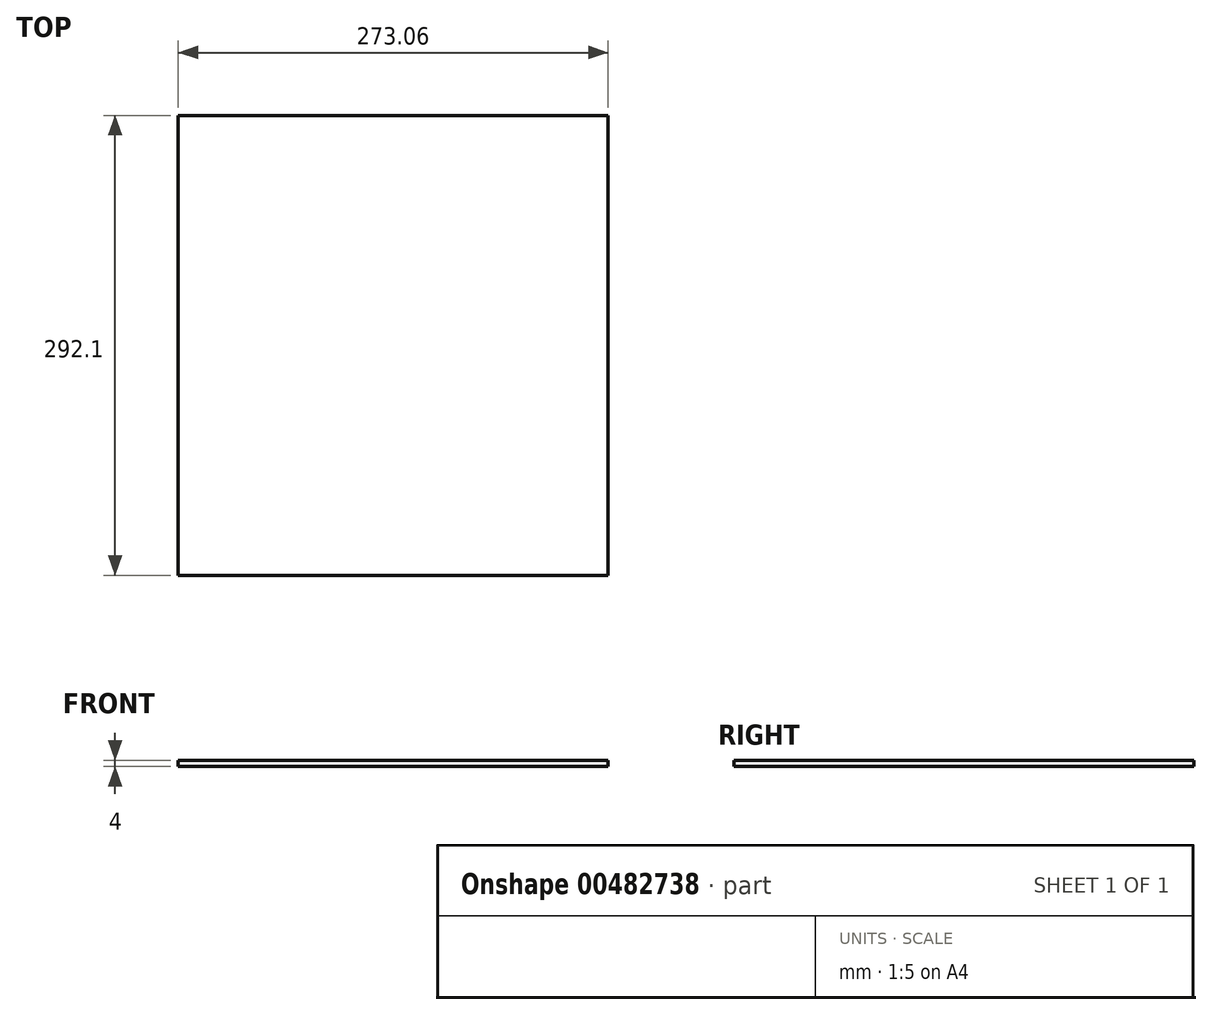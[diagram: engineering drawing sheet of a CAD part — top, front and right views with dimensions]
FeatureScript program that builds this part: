
annotation { "Feature Type Name" : "Feature", "Feature Type Description" : "" }
export const myFeature = defineFeature(function(context is Context, id is Id, definition is map)
    precondition{}
    {
        {
            var Q0;
            Q0=qCreatedBy(makeId("Top.planeOp"),FACE);
            var sketch = newSketch(context, id + "F0", { "sketchPlane" : qUnion([Q0])});
            skLineSegment(sketch, "E0.bottom", {"start": v(136.52, 146.05) * mm, "end": v(-136.53, 146.05) * mm});
            skLineSegment(sketch, "E0.top", {"start": v(136.53, -146.05) * mm, "end": v(-136.52, -146.05) * mm});
            skLineSegment(sketch, "E0.left", {"start": v(136.53, 146.05) * mm, "end": v(136.53, -146.05) * mm});
            skLineSegment(sketch, "E0.right", {"start": v(-136.53, 146.05) * mm, "end": v(-136.52, -146.05) * mm});
            skPoint(sketch, "E0.middle", {"position": v(0, 0) * mm});
            skSolve(sketch);
        }
        {
            var Q0;
            Q0=makeQuery(id+"F0.imprint","IMPRINT",FACE,{"disambiguationData":[TD([[makeQuery(id+"F0.imprint","IMPRINT",EDGE,{"derivedFrom":sQuery(id+"F0.wireOp",EDGE,"E0.bottom")}),1.0]])]});
            extrude(context, id + "F1", {"entities" : qUnion([Q0]), "depth" : 4 * mm});
        }
    });
